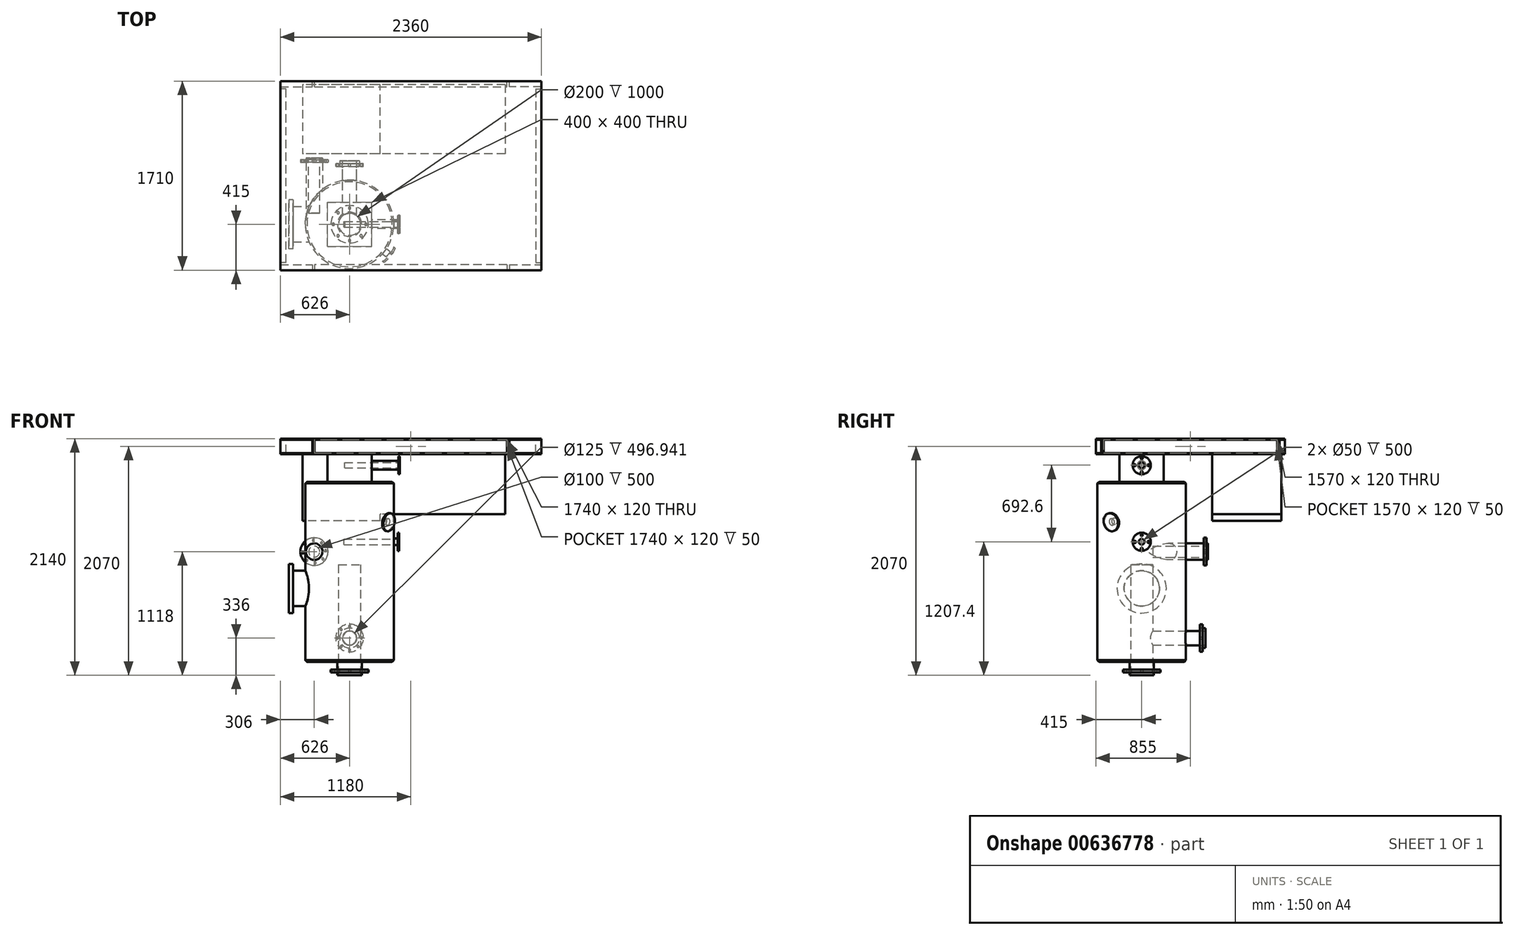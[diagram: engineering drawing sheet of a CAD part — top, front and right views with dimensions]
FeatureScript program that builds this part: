
annotation { "Feature Type Name" : "Feature", "Feature Type Description" : "" }
export const myFeature = defineFeature(function(context is Context, id is Id, definition is map)
    precondition{}
    {
        {
            var Q0;
            Q0=qCreatedBy(makeId("Front.planeOp"),FACE);
            var sketch = newSketch(context, id + "F0", { "sketchPlane" : qUnion([Q0])});
            skLineSegment(sketch, "E0.bottom", {"start": v(0, 0) * mm, "end": v(400, 0) * mm});
            skLineSegment(sketch, "E0.top", {"start": v(0, 1630) * mm, "end": v(400, 1630) * mm});
            skLineSegment(sketch, "E0.left", {"start": v(0, 0) * mm, "end": v(0, 1630) * mm});
            skLineSegment(sketch, "E0.right", {"start": v(400, 0) * mm, "end": v(400, 1630) * mm});
            skSolve(sketch);
        }
        {
            var Q0;
            Q0=makeQuery(id+"F0.imprint","IMPRINT",FACE,{"disambiguationData":[TD([[makeQuery(id+"F0.imprint","IMPRINT",EDGE,{"derivedFrom":sQuery(id+"F0.wireOp",EDGE,"E0.bottom")}),1.0]])]});
            var Q1;
            Q1=sQuery(id+"F0.wireOp",EDGE,"E0.left");
            revolve(context, id + "F1", {"entities" : qUnion([Q0]), "axis" : qUnion([Q1]), "revolveType" : RevolveType.FULL});
        }
        {
            var Q0;
            Q0=makeQuery(id+"F1.opRevolve","SWEPT_EDGE",EDGE,{"disambiguationData":[OSD([sQuery(id+"F0.wireOp",EDGE,"E0.top"),sQuery(id+"F0.wireOp",EDGE,"E0.right")])]});
            chamfer(context, id + "F2", {"entities" : qUnion([Q0]), "width" : 15 * mm, "tangentPropagation" : true});
        }
        {
            var Q0;
            Q0=qCreatedBy(makeId("Front.planeOp"),FACE);
            var sketch = newSketch(context, id + "F3", { "sketchPlane" : qUnion([Q0])});
            skCircle(sketch, "E1", {"center": v(-320, 998) * mm, "radius": 75 * mm});
            skLineSegment(sketch, "E2", {"start": v(-400, 0) * mm, "end": v(-400, 1747) * mm});
            skSolve(sketch);
        }
        {
            var Q0;
            Q0=qSketchRegion(id+"F3",true);
            extrude(context, id + "F4", {"entities" : qUnion([Q0]), "operationType" : NewBodyOperationType.ADD, "oppositeDirection" : true, "depth" : 600 * mm, "offsetDistance" : 25 * mm});
        }
        {
            var Q0;
            Q0=makeQuery(id+"F4.opExtrude","CAP_FACE",FACE,{"disambiguationData":[OSD([sQuery(id+"F3.wireOp",EDGE,"E1")])],"isStart":false});
            cPlane(context, id + "F5", {"entities" : qUnion([Q0]), "cplaneType" : CPlaneType.OFFSET, "offset" : 40 * mm, "oppositeDirection" : true, "width" : 150 * mm, "height" : 150 * mm});
        }
        {
            var Q0;
            Q0=qCreatedBy(id+"F5.planeOp",FACE);
            var sketch = newSketch(context, id + "F6", { "sketchPlane" : qUnion([Q0])});
            skCircle(sketch, "E3", {"center": v(320, 998) * mm, "radius": 125 * mm});
            skSolve(sketch);
        }
        {
            var Q0;
            Q0=makeQuery(id+"F6.imprint","IMPRINT",FACE,{"disambiguationData":[TD([[makeQuery(id+"F6.imprint","IMPRINT",EDGE,{"derivedFrom":sQuery(id+"F6.wireOp",EDGE,"E3")}),1.0]])]});
            extrude(context, id + "F7", {"entities" : qUnion([Q0]), "operationType" : NewBodyOperationType.ADD, "depth" : 25 * mm, "offsetDistance" : 25 * mm});
        }
        {
            var Q0;
            Q0=makeQuery(id+"F7.opExtrude","CAP_FACE",FACE,{"disambiguationData":[OSD([sQuery(id+"F6.wireOp",EDGE,"E3")])],"isStart":false});
            var sketch = newSketch(context, id + "F8", { "sketchPlane" : qUnion([Q0])});
            skCircle(sketch, "E4", {"center": v(311.17, 895.88) * mm, "radius": 9 * mm});
            skCircle(sketch, "E5.1.0", {"center": v(385.96, 919.55) * mm, "radius": 9 * mm});
            skCircle(sketch, "E5.2.0", {"center": v(422.12, 989.17) * mm, "radius": 9 * mm});
            skCircle(sketch, "E5.3.0", {"center": v(398.45, 1063.96) * mm, "radius": 9 * mm});
            skCircle(sketch, "E5.4.0", {"center": v(328.83, 1100.12) * mm, "radius": 9 * mm});
            skCircle(sketch, "E5.5.0", {"center": v(254.04, 1076.45) * mm, "radius": 9 * mm});
            skCircle(sketch, "E5.6.0", {"center": v(217.88, 1006.83) * mm, "radius": 9 * mm});
            skCircle(sketch, "E5.7.0", {"center": v(241.55, 932.04) * mm, "radius": 9 * mm});
            skPoint(sketch, "E5.center", {"position": v(320, 998) * mm});
            skSolve(sketch);
        }
        {
            var Q0;
            Q0=qSketchRegion(id+"F8",true);
            extrude(context, id + "F9", {"entities" : qUnion([Q0]), "operationType" : NewBodyOperationType.REMOVE, "oppositeDirection" : true, "depth" : 25 * mm, "offsetDistance" : 25 * mm});
        }
        {
            var Q0;
            Q0=qCreatedBy(makeId("Right.planeOp"),FACE);
            var sketch = newSketch(context, id + "F10", { "sketchPlane" : qUnion([Q0])});
            skCircle(sketch, "E6", {"center": v(0, 665) * mm, "radius": 160 * mm});
            skSolve(sketch);
        }
        {
            var Q0;
            Q0=qSketchRegion(id+"F10",true);
            extrude(context, id + "F11", {"entities" : qUnion([Q0]), "operationType" : NewBodyOperationType.ADD, "oppositeDirection" : true, "depth" : 550 * mm, "offsetDistance" : 25 * mm});
        }
        {
            var Q0;
            Q0=makeQuery(id+"F11.opExtrude","CAP_FACE",FACE,{"disambiguationData":[OSD([sQuery(id+"F10.wireOp",EDGE,"E6")])],"isStart":false});
            var sketch = newSketch(context, id + "F12", { "sketchPlane" : qUnion([Q0])});
            skCircle(sketch, "E7", {"center": v(0, 665) * mm, "radius": 222.5 * mm});
            skSolve(sketch);
        }
        {
            var Q0;
            Q0=makeQuery(id+"F12.imprint","IMPRINT",FACE,{"disambiguationData":[TD([[makeQuery(id+"F12.imprint","IMPRINT",EDGE,{"derivedFrom":sQuery(id+"F12.wireOp",EDGE,"E7")}),1.0]])]});
            var Q1;
            Q1=makeQuery(id+"F12.imprint","IMPRINT",FACE,{"disambiguationData":[TD([[makeQuery(id+"F12.imprint","IMPRINT",EDGE,{"derivedFrom":makeQuery(id+"F11.opExtrude","CAP_EDGE",EDGE,{"disambiguationData":[OSD([sQuery(id+"F10.wireOp",EDGE,"E6")])],"isStart":false})}),1.0]])]});
            extrude(context, id + "F13", {"entities" : qUnion([Q0, Q1]), "operationType" : NewBodyOperationType.ADD, "oppositeDirection" : true, "depth" : 40 * mm, "offsetDistance" : 25 * mm});
        }
        {
            var Q0;
            Q0=makeQuery(id+"F1.opRevolve","SWEPT_EDGE",EDGE,{"disambiguationData":[OSD([sQuery(id+"F0.wireOp",EDGE,"E0.bottom"),sQuery(id+"F0.wireOp",EDGE,"E0.right")])]});
            chamfer(context, id + "F14", {"entities" : qUnion([Q0]), "width" : 15 * mm, "tangentPropagation" : true});
        }
        {
            var Q0;
            Q0=makeQuery(id+"F1.opRevolve","SWEPT_FACE",FACE,{"disambiguationData":[OSD([sQuery(id+"F0.wireOp",EDGE,"E0.bottom")])]});
            var sketch = newSketch(context, id + "F15", { "sketchPlane" : qUnion([Q0])});
            skCircle(sketch, "E8", {"center": v(0, 0) * mm, "radius": 110 * mm});
            skSolve(sketch);
        }
        {
            var Q0;
            Q0=qSketchRegion(id+"F15",true);
            extrude(context, id + "F16", {"entities" : qUnion([Q0]), "operationType" : NewBodyOperationType.ADD, "depth" : 120 * mm, "offsetDistance" : 25 * mm});
        }
        {
            var Q0;
            Q0=makeQuery(id+"F16.opExtrude","CAP_FACE",FACE,{"disambiguationData":[OSD([sQuery(id+"F15.wireOp",EDGE,"E8")])],"isStart":false});
            cPlane(context, id + "F17", {"entities" : qUnion([Q0]), "cplaneType" : CPlaneType.OFFSET, "offset" : 25 * mm, "oppositeDirection" : true, "width" : 150 * mm, "height" : 150 * mm});
        }
        {
            var Q0;
            Q0=qCreatedBy(id+"F17.planeOp",FACE);
            var sketch = newSketch(context, id + "F18", { "sketchPlane" : qUnion([Q0])});
            skCircle(sketch, "E9", {"center": v(0, 0) * mm, "radius": 170 * mm});
            skSolve(sketch);
        }
        {
            var Q0;
            Q0=qSketchRegion(id+"F18",true);
            extrude(context, id + "F19", {"entities" : qUnion([Q0]), "operationType" : NewBodyOperationType.ADD, "oppositeDirection" : true, "depth" : 25 * mm, "offsetDistance" : 25 * mm});
        }
        {
            var Q0;
            Q0=makeQuery(id+"F19.opExtrude","CAP_FACE",FACE,{"disambiguationData":[OSD([sQuery(id+"F18.wireOp",EDGE,"E9")])],"isStart":true});
            var sketch = newSketch(context, id + "F20", { "sketchPlane" : qUnion([Q0])});
            skCircle(sketch, "E10", {"center": v(0, 147.5) * mm, "radius": 11 * mm});
            skCircle(sketch, "E11.1.0", {"center": v(-104.3, 104.3) * mm, "radius": 11 * mm});
            skCircle(sketch, "E11.2.0", {"center": v(-147.5, 0) * mm, "radius": 11 * mm});
            skCircle(sketch, "E11.3.0", {"center": v(-104.3, -104.3) * mm, "radius": 11 * mm});
            skCircle(sketch, "E11.4.0", {"center": v(0, -147.5) * mm, "radius": 11 * mm});
            skCircle(sketch, "E11.5.0", {"center": v(104.3, -104.3) * mm, "radius": 11 * mm});
            skCircle(sketch, "E11.6.0", {"center": v(147.5, 0) * mm, "radius": 11 * mm});
            skCircle(sketch, "E11.7.0", {"center": v(104.3, 104.3) * mm, "radius": 11 * mm});
            skPoint(sketch, "E11.center", {"position": v(0, 0) * mm});
            skSolve(sketch);
        }
        {
            var Q0;
            Q0=qSketchRegion(id+"F20",true);
            extrude(context, id + "F21", {"entities" : qUnion([Q0]), "operationType" : NewBodyOperationType.REMOVE, "oppositeDirection" : true, "depth" : 25 * mm, "offsetDistance" : 25 * mm});
        }
        {
            var Q0;
            Q0=makeQuery(id+"F1.opRevolve","SWEPT_FACE",FACE,{"disambiguationData":[OSD([sQuery(id+"F0.wireOp",EDGE,"E0.top")])]});
            var sketch = newSketch(context, id + "F22", { "sketchPlane" : qUnion([Q0])});
            skLineSegment(sketch, "E12.bottom", {"start": v(-200, -200) * mm, "end": v(200, -200) * mm});
            skLineSegment(sketch, "E12.top", {"start": v(-200, 200) * mm, "end": v(200, 200) * mm});
            skLineSegment(sketch, "E12.left", {"start": v(-200, -200) * mm, "end": v(-200, 200) * mm});
            skLineSegment(sketch, "E12.right", {"start": v(200, -200) * mm, "end": v(200, 200) * mm});
            skPoint(sketch, "E12.middle", {"position": v(0, 0) * mm});
            skSolve(sketch);
        }
        {
            var Q0;
            Q0=qSketchRegion(id+"F22",true);
            extrude(context, id + "F23", {"entities" : qUnion([Q0]), "operationType" : NewBodyOperationType.ADD, "depth" : 250 * mm, "offsetDistance" : 25 * mm});
        }
        {
            var Q0;
            Q0=makeQuery(id+"F23.opExtrude","CAP_FACE",FACE,{"disambiguationData":[OSD([sQuery(id+"F22.wireOp",EDGE,"E12.bottom"),sQuery(id+"F22.wireOp",EDGE,"E12.top"),sQuery(id+"F22.wireOp",EDGE,"E12.left"),sQuery(id+"F22.wireOp",EDGE,"E12.right")])],"isStart":false});
            var sketch = newSketch(context, id + "F24", { "sketchPlane" : qUnion([Q0])});
            skLineSegment(sketch, "E13.bottom", {"start": v(-626, 1295) * mm, "end": v(1734, 1295) * mm});
            skLineSegment(sketch, "E13.top", {"start": v(-626, -415) * mm, "end": v(1734, -415) * mm});
            skLineSegment(sketch, "E13.left", {"start": v(-626, 1295) * mm, "end": v(-626, -415) * mm});
            skLineSegment(sketch, "E13.right", {"start": v(1734, 1295) * mm, "end": v(1734, -415) * mm});
            skSolve(sketch);
        }
        {
            var Q0;
            Q0=qSketchRegion(id+"F24",true);
            extrude(context, id + "F25", {"entities" : qUnion([Q0]), "operationType" : NewBodyOperationType.ADD, "depth" : 140 * mm, "offsetDistance" : 25 * mm});
        }
        {
            var Q0;
            Q0=qCreatedBy(makeId("Front.planeOp"),FACE);
            var sketch = newSketch(context, id + "F26", { "sketchPlane" : qUnion([Q0])});
            skLineSegment(sketch, "E14", {"start": v(0, 0) * mm, "end": v(0, -161.72) * mm});
            skSolve(sketch);
        }
        {
            var Q0;
            Q0=sQuery(id+"F26.wireOp",EDGE,"E14");
            cPlane(context, id + "F27", {"entities" : qUnion([Q0]), "cplaneType" : CPlaneType.LINE_ANGLE, "offset" : 25 * mm, "angle" : 38 * degree, "width" : 150 * mm, "height" : 150 * mm});
        }
        {
            var Q0;
            Q0=qCreatedBy(id+"F27.planeOp",FACE);
            cPlane(context, id + "F28", {"entities" : qUnion([Q0]), "cplaneType" : CPlaneType.OFFSET, "offset" : 340 * mm, "oppositeDirection" : true, "width" : 150 * mm, "height" : 150 * mm});
        }
        {
            var Q0;
            Q0=qCreatedBy(id+"F28.planeOp",FACE);
            var sketch = newSketch(context, id + "F29", { "sketchPlane" : qUnion([Q0])});
            skLineSegment(sketch, "E15", {"start": v(0, 1281.3) * mm, "end": v(148.15, 1281.3) * mm});
            skSolve(sketch);
        }
        {
            var Q0;
            Q0=sQuery(id+"F29.wireOp",EDGE,"E15");
            cPlane(context, id + "F30", {"entities" : qUnion([Q0]), "cplaneType" : CPlaneType.LINE_ANGLE, "offset" : 25 * mm, "angle" : 80 * degree, "width" : 150 * mm, "height" : 150 * mm});
        }
        {
            var Q0;
            Q0=qCreatedBy(id+"F30.planeOp",FACE);
            var sketch = newSketch(context, id + "F31", { "sketchPlane" : qUnion([Q0])});
            skCircle(sketch, "E16", {"center": v(-177.95, 1311.44) * mm, "radius": 30 * mm});
            skSolve(sketch);
        }
        {
            var Q0;
            Q0=qSketchRegion(id+"F31",true);
            extrude(context, id + "F32", {"entities" : qUnion([Q0]), "operationType" : NewBodyOperationType.ADD, "depth" : 100 * mm, "offsetDistance" : 25 * mm});
        }
        {
            var Q0;
            Q0=makeQuery(id+"F32.opExtrude","CAP_FACE",FACE,{"disambiguationData":[OSD([sQuery(id+"F31.wireOp",EDGE,"E16")])],"isStart":false});
            var sketch = newSketch(context, id + "F33", { "sketchPlane" : qUnion([Q0])});
            skCircle(sketch, "E17", {"center": v(-177.95, 1311.44) * mm, "radius": 82.5 * mm});
            skSolve(sketch);
        }
        {
            var Q0;
            Q0=qSketchRegion(id+"F33",true);
            extrude(context, id + "F34", {"entities" : qUnion([Q0]), "operationType" : NewBodyOperationType.ADD, "depth" : 15 * mm, "offsetDistance" : 25 * mm});
        }
        {
            var Q0;
            Q0=makeQuery(id+"F25.opExtrude","SWEPT_FACE",FACE,{"disambiguationData":[OSD([sQuery(id+"F24.wireOp",EDGE,"E13.bottom")])]});
            var sketch = newSketch(context, id + "F35", { "sketchPlane" : qUnion([Q0])});
            skLineSegment(sketch, "E18.bottom", {"start": v(316, 1890) * mm, "end": v(-1424, 1890) * mm});
            skLineSegment(sketch, "E18.top", {"start": v(316, 2010) * mm, "end": v(-1424, 2010) * mm});
            skLineSegment(sketch, "E18.left", {"start": v(316, 1890) * mm, "end": v(316, 2010) * mm});
            skLineSegment(sketch, "E18.right", {"start": v(-1424, 1890) * mm, "end": v(-1424, 2010) * mm});
            skLineSegment(sketch, "E19.bottom", {"start": v(626, 1890) * mm, "end": v(336, 1890) * mm});
            skLineSegment(sketch, "E19.top", {"start": v(626, 2010) * mm, "end": v(336, 2010) * mm});
            skLineSegment(sketch, "E19.left", {"start": v(626, 1890) * mm, "end": v(626, 2010) * mm});
            skLineSegment(sketch, "E19.right", {"start": v(336, 1890) * mm, "end": v(336, 2010) * mm});
            skLineSegment(sketch, "E20.bottom", {"start": v(-1734, 1890) * mm, "end": v(-1444, 1890) * mm});
            skLineSegment(sketch, "E20.top", {"start": v(-1734, 2010) * mm, "end": v(-1444, 2010) * mm});
            skLineSegment(sketch, "E20.left", {"start": v(-1734, 1890) * mm, "end": v(-1734, 2010) * mm});
            skLineSegment(sketch, "E20.right", {"start": v(-1444, 1890) * mm, "end": v(-1444, 2010) * mm});
            skSolve(sketch);
        }
        {
            var Q0;
            Q0=qSketchRegion(id+"F35",true);
            extrude(context, id + "F36", {"entities" : qUnion([Q0]), "operationType" : NewBodyOperationType.REMOVE, "oppositeDirection" : true, "depth" : 50 * mm, "offsetDistance" : 25 * mm});
        }
        {
            var Q0;
            Q0=makeQuery(id+"F25.opExtrude","SWEPT_FACE",FACE,{"disambiguationData":[OSD([sQuery(id+"F24.wireOp",EDGE,"E13.top")])]});
            var sketch = newSketch(context, id + "F37", { "sketchPlane" : qUnion([Q0])});
            skLineSegment(sketch, "E21.0.0", {"start": v(1444, 2010) * mm, "end": v(1734, 2010) * mm});
            skLineSegment(sketch, "E21.0.1", {"start": v(1734, 2010) * mm, "end": v(1734, 1890) * mm});
            skLineSegment(sketch, "E21.0.2", {"start": v(1734, 1890) * mm, "end": v(1444, 1890) * mm});
            skLineSegment(sketch, "E21.0.3", {"start": v(1444, 1890) * mm, "end": v(1444, 2010) * mm});
            skLineSegment(sketch, "E22.0.0", {"start": v(-316, 1890) * mm, "end": v(-316, 2010) * mm});
            skLineSegment(sketch, "E22.0.1", {"start": v(-316, 2010) * mm, "end": v(1424, 2010) * mm});
            skLineSegment(sketch, "E22.0.2", {"start": v(1424, 2010) * mm, "end": v(1424, 1890) * mm});
            skLineSegment(sketch, "E22.0.3", {"start": v(1424, 1890) * mm, "end": v(-316, 1890) * mm});
            skLineSegment(sketch, "E23.0.0", {"start": v(-626, 1890) * mm, "end": v(-626, 2010) * mm});
            skLineSegment(sketch, "E23.0.1", {"start": v(-626, 2010) * mm, "end": v(-336, 2010) * mm});
            skLineSegment(sketch, "E23.0.2", {"start": v(-336, 2010) * mm, "end": v(-336, 1890) * mm});
            skLineSegment(sketch, "E23.0.3", {"start": v(-336, 1890) * mm, "end": v(-626, 1890) * mm});
            skSolve(sketch);
        }
        {
            var Q0;
            Q0=qSketchRegion(id+"F37",true);
            extrude(context, id + "F38", {"entities" : qUnion([Q0]), "operationType" : NewBodyOperationType.REMOVE, "oppositeDirection" : true, "depth" : 50 * mm, "offsetDistance" : 25 * mm});
        }
        {
            var Q0;
            Q0=makeQuery(id+"F25.opExtrude","SWEPT_FACE",FACE,{"disambiguationData":[OSD([sQuery(id+"F24.wireOp",EDGE,"E13.right")])]});
            var sketch = newSketch(context, id + "F39", { "sketchPlane" : qUnion([Q0])});
            skLineSegment(sketch, "E24.bottom", {"start": v(1225, 1890) * mm, "end": v(-345, 1890) * mm});
            skLineSegment(sketch, "E24.top", {"start": v(1225, 2010) * mm, "end": v(-345, 2010) * mm});
            skLineSegment(sketch, "E24.left", {"start": v(1225, 1890) * mm, "end": v(1225, 2010) * mm});
            skLineSegment(sketch, "E24.right", {"start": v(-345, 1890) * mm, "end": v(-345, 2010) * mm});
            skSolve(sketch);
        }
        {
            var Q0;
            Q0=makeQuery(id+"F39.imprint","IMPRINT",FACE,{"disambiguationData":[TD([[makeQuery(id+"F39.imprint","IMPRINT",EDGE,{"derivedFrom":sQuery(id+"F39.wireOp",EDGE,"E24.bottom")}),-1.0]])]});
            extrude(context, id + "F40", {"entities" : qUnion([Q0]), "operationType" : NewBodyOperationType.REMOVE, "oppositeDirection" : true, "depth" : 50 * mm, "offsetDistance" : 25 * mm});
        }
        {
            var Q0;
            Q0=makeQuery(id+"F25.opExtrude","SWEPT_FACE",FACE,{"disambiguationData":[OSD([sQuery(id+"F24.wireOp",EDGE,"E13.left")])]});
            var sketch = newSketch(context, id + "F41", { "sketchPlane" : qUnion([Q0])});
            skLineSegment(sketch, "E25.0.0", {"start": v(-1225, 1890) * mm, "end": v(-1225, 2010) * mm});
            skLineSegment(sketch, "E25.0.1", {"start": v(-1225, 2010) * mm, "end": v(345, 2010) * mm});
            skLineSegment(sketch, "E25.0.2", {"start": v(345, 2010) * mm, "end": v(345, 1890) * mm});
            skLineSegment(sketch, "E25.0.3", {"start": v(345, 1890) * mm, "end": v(-1225, 1890) * mm});
            skSolve(sketch);
        }
        {
            var Q0;
            Q0=makeQuery(id+"F41.imprint","IMPRINT",FACE,{"disambiguationData":[TD([[makeQuery(id+"F41.imprint","IMPRINT",EDGE,{"derivedFrom":sQuery(id+"F41.wireOp",EDGE,"E25.0.0")}),-1.0]])]});
            extrude(context, id + "F42", {"entities" : qUnion([Q0]), "operationType" : NewBodyOperationType.REMOVE, "oppositeDirection" : true, "depth" : 50 * mm, "offsetDistance" : 25 * mm});
        }
        {
            var Q0;
            Q0=makeQuery(id+"F23.opExtrude","SWEPT_FACE",FACE,{"disambiguationData":[OSD([sQuery(id+"F22.wireOp",EDGE,"E12.right")])]});
            var sketch = newSketch(context, id + "F43", { "sketchPlane" : qUnion([Q0])});
            skCircle(sketch, "E26", {"center": v(0, 1780) * mm, "radius": 40 * mm});
            skSolve(sketch);
        }
        {
            var Q0;
            Q0=makeQuery(id+"F43.imprint","IMPRINT",FACE,{"disambiguationData":[TD([[makeQuery(id+"F43.imprint","IMPRINT",EDGE,{"derivedFrom":sQuery(id+"F43.wireOp",EDGE,"E26")}),1.0]])]});
            extrude(context, id + "F44", {"entities" : qUnion([Q0]), "operationType" : NewBodyOperationType.ADD, "depth" : 240 * mm, "offsetDistance" : 25 * mm});
        }
        {
            var Q0;
            Q0=makeQuery(id+"F44.opExtrude","CAP_FACE",FACE,{"disambiguationData":[OSD([sQuery(id+"F43.wireOp",EDGE,"E26")])],"isStart":false});
            var sketch = newSketch(context, id + "F45", { "sketchPlane" : qUnion([Q0])});
            skCircle(sketch, "E27", {"center": v(0, 1780) * mm, "radius": 82.5 * mm});
            skSolve(sketch);
        }
        {
            var Q0;
            Q0=qSketchRegion(id+"F45",true);
            extrude(context, id + "F46", {"entities" : qUnion([Q0]), "operationType" : NewBodyOperationType.ADD, "depth" : 15 * mm, "offsetDistance" : 25 * mm});
        }
        {
            var Q0;
            Q0=makeQuery(id+"F46.opExtrude","CAP_FACE",FACE,{"disambiguationData":[OSD([sQuery(id+"F45.wireOp",EDGE,"E27")])],"isStart":false});
            var sketch = newSketch(context, id + "F47", { "sketchPlane" : qUnion([Q0])});
            skCircle(sketch, "E28", {"center": v(0, 1717.5) * mm, "radius": 9 * mm});
            skCircle(sketch, "E29.1.0", {"center": v(62.5, 1780) * mm, "radius": 9 * mm});
            skCircle(sketch, "E29.2.0", {"center": v(0, 1842.5) * mm, "radius": 9 * mm});
            skCircle(sketch, "E29.3.0", {"center": v(-62.5, 1780) * mm, "radius": 9 * mm});
            skPoint(sketch, "E29.center", {"position": v(0, 1780) * mm});
            skSolve(sketch);
        }
        {
            var Q0;
            Q0=qSketchRegion(id+"F47",true);
            extrude(context, id + "F48", {"entities" : qUnion([Q0]), "operationType" : NewBodyOperationType.REMOVE, "oppositeDirection" : true, "depth" : 25 * mm, "offsetDistance" : 25 * mm});
        }
        {
            var Q0;
            Q0=makeQuery(id+"F46.opExtrude","CAP_FACE",FACE,{"disambiguationData":[OSD([sQuery(id+"F45.wireOp",EDGE,"E27")])],"isStart":false});
            var sketch = newSketch(context, id + "F49", { "sketchPlane" : qUnion([Q0])});
            skCircle(sketch, "E30", {"center": v(0, 1780) * mm, "radius": 25 * mm});
            skSolve(sketch);
        }
        {
            var Q0;
            Q0=makeQuery(id+"F49.imprint","IMPRINT",FACE,{"disambiguationData":[TD([[makeQuery(id+"F49.imprint","IMPRINT",EDGE,{"derivedFrom":sQuery(id+"F49.wireOp",EDGE,"E30")}),1.0]])]});
            extrude(context, id + "F50", {"entities" : qUnion([Q0]), "operationType" : NewBodyOperationType.REMOVE, "oppositeDirection" : true, "depth" : 500 * mm, "offsetDistance" : 25 * mm});
        }
        {
            var Q0;
            Q0=qCreatedBy(makeId("Front.planeOp"),FACE);
            var sketch = newSketch(context, id + "F51", { "sketchPlane" : qUnion([Q0])});
            skCircle(sketch, "E31", {"center": v(0, 216) * mm, "radius": 65 * mm});
            skSolve(sketch);
        }
        {
            var Q0;
            Q0=makeQuery(id+"F25.opExtrude","CAP_FACE",FACE,{"disambiguationData":[OSD([sQuery(id+"F24.wireOp",EDGE,"E13.bottom"),sQuery(id+"F24.wireOp",EDGE,"E13.top"),sQuery(id+"F24.wireOp",EDGE,"E13.left"),sQuery(id+"F24.wireOp",EDGE,"E13.right")])],"isStart":false});
            cPlane(context, id + "F52", {"entities" : qUnion([Q0]), "cplaneType" : CPlaneType.OFFSET, "offset" : 1804 * mm, "oppositeDirection" : true, "width" : 150 * mm, "height" : 150 * mm});
        }
        {
            var Q0;
            Q0=qCreatedBy(id+"F52.planeOp",FACE);
            var sketch = newSketch(context, id + "F53", { "sketchPlane" : qUnion([Q0])});
            skLineSegment(sketch, "E32", {"start": v(0, 0) * mm, "end": v(0, 550) * mm});
            skSolve(sketch);
        }
        {
            var Q0;
            Q0 = qSketchRegion(id + "F51", true);
            var Q1;
            Q1=sQuery(id+"F53.wireOp",EDGE,"E32");
            sweep(context, id + "F54", {"operationType" : NewBodyOperationType.ADD, "profiles" : qUnion([Q0]), "path" : qUnion([Q1])});
        }
        {
            var Q0;
            Q0=makeQuery(id+"F54.opSweep","CAP_FACE",FACE,{"disambiguationData":[OSD([sQuery(id+"F51.wireOp",EDGE,"E31"),sQuery(id+"F53.wireOp",VERTEX,"E32.end")])],"isStart":false});
            var sketch = newSketch(context, id + "F55", { "sketchPlane" : qUnion([Q0])});
            skCircle(sketch, "E33", {"center": v(0, 216) * mm, "radius": 125 * mm});
            skSolve(sketch);
        }
        {
            var Q0;
            Q0=makeQuery(id+"F55.imprint","IMPRINT",FACE,{"disambiguationData":[TD([[makeQuery(id+"F55.imprint","IMPRINT",EDGE,{"derivedFrom":sQuery(id+"F55.wireOp",EDGE,"E33")}),1.0]])]});
            extrude(context, id + "F56", {"entities" : qUnion([Q0]), "operationType" : NewBodyOperationType.ADD, "oppositeDirection" : true, "depth" : 25 * mm, "offsetDistance" : 25 * mm});
        }
        {
            var Q0;
            {var subQ0=sQuery(id+"F53.wireOp",VERTEX,"E32.end");var subQ1=sQuery(id+"F51.wireOp",EDGE,"E31");Q0=makeQuery(id+"F56.boolean.opBoolean","MERGE",FACE,{"derivedFrom":[makeQuery(id+"F54.opSweep","CAP_FACE",FACE,{"disambiguationData":[OSD([subQ1,subQ0])],"isStart":false}),makeQuery(id+"F56.opExtrude","CAP_FACE",FACE,{"disambiguationData":[OSD([subQ1,subQ0,sQuery(id+"F55.wireOp",EDGE,"E33")])],"isStart":true})]});}
            var sketch = newSketch(context, id + "F57", { "sketchPlane" : qUnion([Q0])});
            skCircle(sketch, "E34", {"center": v(0, 216) * mm, "radius": 90 * mm});
            skSolve(sketch);
        }
        {
            var Q0;
            Q0=makeQuery(id+"F57.imprint","IMPRINT",FACE,{"disambiguationData":[TD([[makeQuery(id+"F57.imprint","IMPRINT",EDGE,{"derivedFrom":sQuery(id+"F57.wireOp",EDGE,"E34")}),1.0]])]});
            var Q1;
            Q1=sQuery(id+"F57.wireOp",EDGE,"E34");
            extrude(context, id + "F58", {"entities" : qUnion([Q0]), "operationType" : NewBodyOperationType.ADD, "surfaceEntities" : qUnion([Q1]), "depth" : 25 * mm, "offsetDistance" : 25 * mm});
        }
        {
            var Q0;
            Q0=makeQuery(id+"F58.opExtrude","CAP_FACE",FACE,{"disambiguationData":[OSD([sQuery(id+"F57.wireOp",EDGE,"E34")])],"isStart":false});
            var sketch = newSketch(context, id + "F59", { "sketchPlane" : qUnion([Q0])});
            skCircle(sketch, "E35", {"center": v(0, 216) * mm, "radius": 62.5 * mm});
            skSolve(sketch);
        }
        {
            var Q0;
            Q0=makeQuery(id+"F59.imprint","IMPRINT",FACE,{"disambiguationData":[TD([[makeQuery(id+"F59.imprint","IMPRINT",EDGE,{"derivedFrom":sQuery(id+"F59.wireOp",EDGE,"E35")}),1.0]])]});
            extrude(context, id + "F60", {"entities" : qUnion([Q0]), "operationType" : NewBodyOperationType.REMOVE, "oppositeDirection" : true, "depth" : 500 * mm, "offsetDistance" : 25 * mm});
        }
        {
            var Q0;
            {var subQ0=sQuery(id+"F53.wireOp",VERTEX,"E32.end");var subQ1=sQuery(id+"F51.wireOp",EDGE,"E31");Q0=makeQuery(id+"F56.boolean.opBoolean","MERGE",FACE,{"derivedFrom":[makeQuery(id+"F54.opSweep","CAP_FACE",FACE,{"disambiguationData":[OSD([subQ1,subQ0])],"isStart":false}),makeQuery(id+"F56.opExtrude","CAP_FACE",FACE,{"disambiguationData":[OSD([subQ1,subQ0,sQuery(id+"F55.wireOp",EDGE,"E33")])],"isStart":true})]});}
            var sketch = newSketch(context, id + "F61", { "sketchPlane" : qUnion([Q0])});
            skCircle(sketch, "E36", {"center": v(0, 108.53) * mm, "radius": 9 * mm});
            skCircle(sketch, "E37.1.0", {"center": v(76, 140) * mm, "radius": 9 * mm});
            skCircle(sketch, "E37.2.0", {"center": v(107.47, 216) * mm, "radius": 9 * mm});
            skCircle(sketch, "E37.3.0", {"center": v(76, 292) * mm, "radius": 9 * mm});
            skCircle(sketch, "E37.4.0", {"center": v(0, 323.47) * mm, "radius": 9 * mm});
            skCircle(sketch, "E37.5.0", {"center": v(-76, 292) * mm, "radius": 9 * mm});
            skCircle(sketch, "E37.6.0", {"center": v(-107.47, 216) * mm, "radius": 9 * mm});
            skCircle(sketch, "E37.7.0", {"center": v(-76, 140) * mm, "radius": 9 * mm});
            skPoint(sketch, "E37.center", {"position": v(0, 216) * mm});
            skSolve(sketch);
        }
        {
            var Q0;
            Q0 = qSketchRegion(id + "F61", true);
            extrude(context, id + "F62", {"entities" : qUnion([Q0]), "operationType" : NewBodyOperationType.REMOVE, "oppositeDirection" : true, "depth" : 25 * mm, "offsetDistance" : 25 * mm});
        }
        {
            var Q0;
            Q0=makeQuery(id+"F4.opExtrude","CAP_FACE",FACE,{"disambiguationData":[OSD([sQuery(id+"F3.wireOp",EDGE,"E1")])],"isStart":false});
            var sketch = newSketch(context, id + "F63", { "sketchPlane" : qUnion([Q0])});
            skCircle(sketch, "E38", {"center": v(320, 998) * mm, "radius": 50 * mm});
            skSolve(sketch);
        }
        {
            var Q0;
            Q0=makeQuery(id+"F63.imprint","IMPRINT",FACE,{"disambiguationData":[TD([[makeQuery(id+"F63.imprint","IMPRINT",EDGE,{"derivedFrom":sQuery(id+"F63.wireOp",EDGE,"E38")}),1.0]])]});
            extrude(context, id + "F64", {"entities" : qUnion([Q0]), "operationType" : NewBodyOperationType.REMOVE, "oppositeDirection" : true, "depth" : 500 * mm, "offsetDistance" : 25 * mm});
        }
        {
            var Q0;
            Q0=makeQuery(id+"F16.opExtrude","CAP_FACE",FACE,{"disambiguationData":[OSD([sQuery(id+"F15.wireOp",EDGE,"E8")])],"isStart":false});
            var sketch = newSketch(context, id + "F65", { "sketchPlane" : qUnion([Q0])});
            skCircle(sketch, "E39", {"center": v(0, 0) * mm, "radius": 100 * mm});
            skSolve(sketch);
        }
        {
            var Q0;
            Q0=makeQuery(id+"F65.imprint","IMPRINT",FACE,{"disambiguationData":[TD([[makeQuery(id+"F65.imprint","IMPRINT",EDGE,{"derivedFrom":sQuery(id+"F65.wireOp",EDGE,"E39")}),1.0]])]});
            extrude(context, id + "F66", {"entities" : qUnion([Q0]), "operationType" : NewBodyOperationType.REMOVE, "oppositeDirection" : true, "depth" : 1000 * mm, "offsetDistance" : 25 * mm});
        }
        {
            var Q0;
            Q0=makeQuery(id+"F25.opExtrude","CAP_FACE",FACE,{"disambiguationData":[OSD([sQuery(id+"F24.wireOp",EDGE,"E13.bottom"),sQuery(id+"F24.wireOp",EDGE,"E13.top"),sQuery(id+"F24.wireOp",EDGE,"E13.left"),sQuery(id+"F24.wireOp",EDGE,"E13.right")])],"isStart":true});
            var sketch = newSketch(context, id + "F67", { "sketchPlane" : qUnion([Q0])});
            skLineSegment(sketch, "E40.bottom", {"start": v(1406, -1264) * mm, "end": v(-425, -1264) * mm});
            skLineSegment(sketch, "E40.top", {"start": v(1406, -638) * mm, "end": v(-425, -638) * mm});
            skLineSegment(sketch, "E40.left", {"start": v(1406, -1264) * mm, "end": v(1406, -638) * mm});
            skLineSegment(sketch, "E40.right", {"start": v(-425, -1264) * mm, "end": v(-425, -638) * mm});
            skSolve(sketch);
        }
        {
            var Q0;
            Q0=makeQuery(id+"F67.imprint","IMPRINT",FACE,{"disambiguationData":[TD([[makeQuery(id+"F67.imprint","IMPRINT",EDGE,{"derivedFrom":sQuery(id+"F67.wireOp",EDGE,"E40.bottom")}),-1.0]])]});
            extrude(context, id + "F68", {"entities" : qUnion([Q0]), "operationType" : NewBodyOperationType.ADD, "depth" : 542 * mm, "offsetDistance" : 25 * mm});
        }
        {
            var Q0;
            Q0=makeQuery(id+"F68.opExtrude","CAP_FACE",FACE,{"disambiguationData":[OSD([sQuery(id+"F67.wireOp",EDGE,"E40.bottom"),sQuery(id+"F67.wireOp",EDGE,"E40.top"),sQuery(id+"F67.wireOp",EDGE,"E40.left"),sQuery(id+"F67.wireOp",EDGE,"E40.right")])],"isStart":false});
            var sketch = newSketch(context, id + "F69", { "sketchPlane" : qUnion([Q0])});
            skLineSegment(sketch, "E41.bottom", {"start": v(-425, -638) * mm, "end": v(275, -638) * mm});
            skLineSegment(sketch, "E41.top", {"start": v(-425, -1264) * mm, "end": v(275, -1264) * mm});
            skLineSegment(sketch, "E41.left", {"start": v(-425, -638) * mm, "end": v(-425, -1264) * mm});
            skLineSegment(sketch, "E41.right", {"start": v(275, -638) * mm, "end": v(275, -1264) * mm});
            skSolve(sketch);
        }
        {
            var Q0;
            Q0=makeQuery(id+"F69.imprint","IMPRINT",FACE,{"disambiguationData":[TD([[makeQuery(id+"F69.imprint","IMPRINT",EDGE,{"derivedFrom":sQuery(id+"F69.wireOp",EDGE,"E41.bottom")}),1.0]])]});
            extrude(context, id + "F70", {"entities" : qUnion([Q0]), "operationType" : NewBodyOperationType.ADD, "depth" : 61.2 * mm, "offsetDistance" : 25 * mm});
        }
        {
            var Q0;
            Q0=qCreatedBy(makeId("Right.planeOp"),FACE);
            var sketch = newSketch(context, id + "F71", { "sketchPlane" : qUnion([Q0])});
            skCircle(sketch, "E42", {"center": v(0, 1087.4) * mm, "radius": 30 * mm});
            skSolve(sketch);
        }
        {
            var Q0;
            Q0 = qSketchRegion(id + "F71", true);
            extrude(context, id + "F72", {"entities" : qUnion([Q0]), "operationType" : NewBodyOperationType.ADD, "depth" : 448.5 * mm, "offsetDistance" : 25 * mm});
        }
        {
            var Q0;
            Q0=makeQuery(id+"F72.opExtrude","CAP_FACE",FACE,{"disambiguationData":[OSD([sQuery(id+"F71.wireOp",EDGE,"E42")])],"isStart":false});
            var sketch = newSketch(context, id + "F73", { "sketchPlane" : qUnion([Q0])});
            skCircle(sketch, "E43", {"center": v(0, 1087.4) * mm, "radius": 82.5 * mm});
            skSolve(sketch);
        }
        {
            var Q0;
            Q0=makeQuery(id+"F73.imprint","IMPRINT",FACE,{"disambiguationData":[TD([[makeQuery(id+"F73.imprint","IMPRINT",EDGE,{"derivedFrom":sQuery(id+"F73.wireOp",EDGE,"E43")}),1.0]])]});
            extrude(context, id + "F74", {"entities" : qUnion([Q0]), "operationType" : NewBodyOperationType.ADD, "oppositeDirection" : true, "depth" : 15 * mm, "offsetDistance" : 25 * mm});
        }
        {
            var Q0;
            {var subQ0=sQuery(id+"F71.wireOp",EDGE,"E42");Q0=makeQuery(id+"F74.boolean.opBoolean","MERGE",FACE,{"derivedFrom":[makeQuery(id+"F72.opExtrude","CAP_FACE",FACE,{"disambiguationData":[OSD([subQ0])],"isStart":false}),makeQuery(id+"F74.opExtrude","CAP_FACE",FACE,{"disambiguationData":[OSD([subQ0,sQuery(id+"F73.wireOp",EDGE,"E43")])],"isStart":true})]});}
            var sketch = newSketch(context, id + "F75", { "sketchPlane" : qUnion([Q0])});
            skCircle(sketch, "E44", {"center": v(0, 1087.4) * mm, "radius": 25 * mm});
            skSolve(sketch);
        }
        {
            var Q0;
            Q0=makeQuery(id+"F75.imprint","IMPRINT",FACE,{"disambiguationData":[TD([[makeQuery(id+"F75.imprint","IMPRINT",EDGE,{"derivedFrom":sQuery(id+"F75.wireOp",EDGE,"E44")}),1.0]])]});
            extrude(context, id + "F76", {"entities" : qUnion([Q0]), "operationType" : NewBodyOperationType.REMOVE, "oppositeDirection" : true, "depth" : 500 * mm, "offsetDistance" : 25 * mm});
        }
        {
            var Q0;
            {var subQ0=sQuery(id+"F71.wireOp",EDGE,"E42");Q0=makeQuery(id+"F74.boolean.opBoolean","MERGE",FACE,{"derivedFrom":[makeQuery(id+"F72.opExtrude","CAP_FACE",FACE,{"disambiguationData":[OSD([subQ0])],"isStart":false}),makeQuery(id+"F74.opExtrude","CAP_FACE",FACE,{"disambiguationData":[OSD([subQ0,sQuery(id+"F73.wireOp",EDGE,"E43")])],"isStart":true})]});}
            var sketch = newSketch(context, id + "F77", { "sketchPlane" : qUnion([Q0])});
            skSolve(sketch);
        }
        {
            var Q0;
            Q0=makeQuery(id+"F77.imprint","IMPRINT",FACE,{"disambiguationData":[TD([[makeQuery(id+"F77.imprint","IMPRINT",EDGE,{"derivedFrom":makeQuery(id+"F74.opExtrude","CAP_EDGE",EDGE,{"disambiguationData":[OSD([sQuery(id+"F73.wireOp",EDGE,"E43")])],"isStart":true})}),1.0]])]});
            var sketch = newSketch(context, id + "F78", { "sketchPlane" : qUnion([Q0])});
            skCircle(sketch, "E45", {"center": v(0, 1024.9) * mm, "radius": 9 * mm});
            skCircle(sketch, "E46.1.0", {"center": v(61.1, 1086) * mm, "radius": 9 * mm});
            skCircle(sketch, "E46.2.0", {"center": v(0, 1147.1) * mm, "radius": 9 * mm});
            skCircle(sketch, "E46.3.0", {"center": v(-61.1, 1086) * mm, "radius": 9 * mm});
            skPoint(sketch, "E46.center", {"position": v(0, 1086) * mm});
            skSolve(sketch);
        }
        {
            var Q0;
            Q0 = qSketchRegion(id + "F78", true);
            extrude(context, id + "F79", {"entities" : qUnion([Q0]), "operationType" : NewBodyOperationType.REMOVE, "oppositeDirection" : true, "depth" : 25 * mm, "offsetDistance" : 25 * mm});
        }
    });
